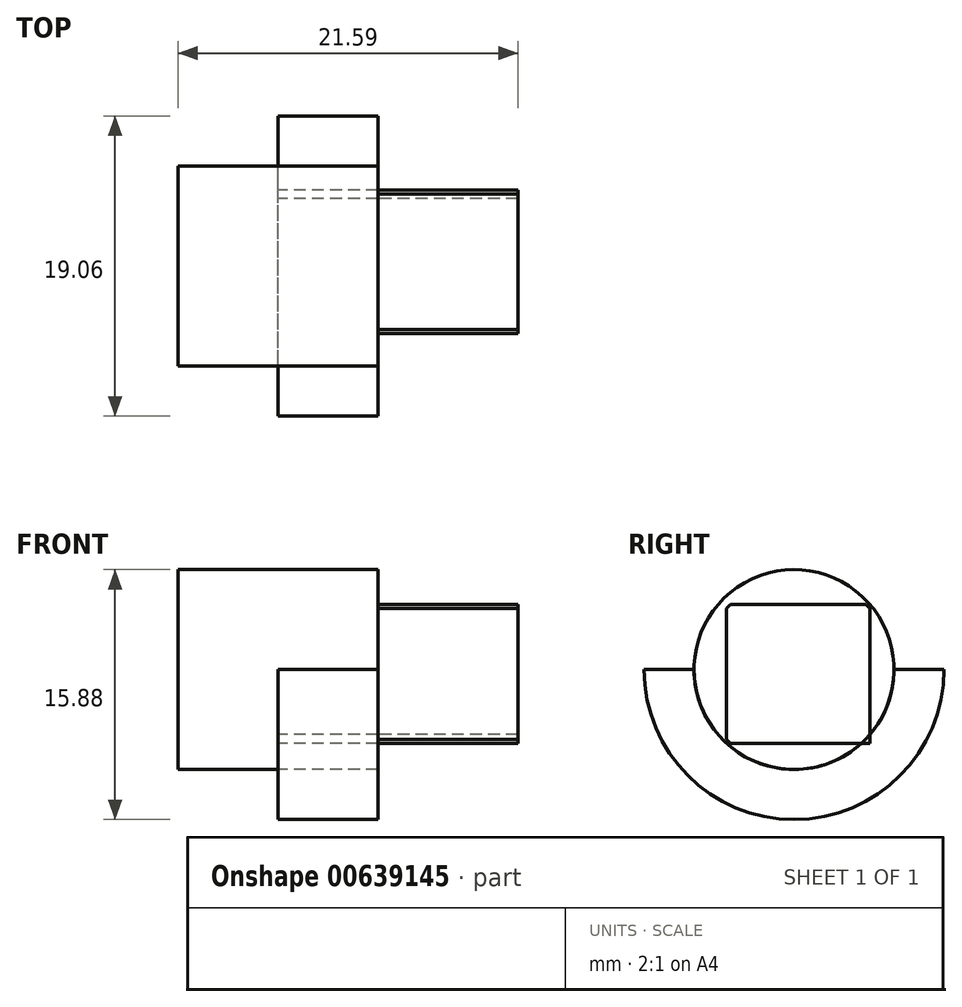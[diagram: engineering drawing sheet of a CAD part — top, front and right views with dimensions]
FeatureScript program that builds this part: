
annotation { "Feature Type Name" : "Feature", "Feature Type Description" : "" }
export const myFeature = defineFeature(function(context is Context, id is Id, definition is map)
    precondition{}
    {
        {
            var Q0;
            Q0=qCreatedBy(makeId("Right.planeOp"),FACE);
            var sketch = newSketch(context, id + "F0", { "sketchPlane" : qUnion([Q0])});
            skCircle(sketch, "E0.0", {"center": v(0, 0) * mm, "radius": 9.53 * mm});
            skLineSegment(sketch, "E1", {"start": v(0, 15.48) * mm, "end": v(0, -15.3) * mm});
            skLineSegment(sketch, "E2", {"start": v(-13.6, 0) * mm, "end": v(13.58, 0) * mm});
            skArc(sketch, "E3", {"start": v(4.83, 4.12) * mm, "mid": v(-4.4, 4.57) * mm, "end": v(-4.3, -4.68) * mm});
            skArc(sketch, "E4", {"start": v(3.74, -5.13) * mm, "mid": v(6.3, -0.75) * mm, "end": v(4.83, 4.12) * mm});
            skArc(sketch, "E5", {"start": v(-3.35, -5.4) * mm, "mid": v(0.23, -6.35) * mm, "end": v(3.74, -5.13) * mm});
            skArc(sketch, "E6", {"start": v(-4.3, -4.68) * mm, "mid": v(-3.84, -5.06) * mm, "end": v(-3.35, -5.4) * mm});
            skLineSegment(sketch, "E7.bottom", {"start": v(-4.3, -4.68) * mm, "end": v(4.83, -4.68) * mm});
            skLineSegment(sketch, "E7.top", {"start": v(-4.3, 4.12) * mm, "end": v(4.83, 4.12) * mm});
            skLineSegment(sketch, "E7.left", {"start": v(-4.3, -4.68) * mm, "end": v(-4.3, 4.12) * mm});
            skLineSegment(sketch, "E7.right", {"start": v(4.83, -4.68) * mm, "end": v(4.83, 4.12) * mm});
            skSolve(sketch);
        }
        {
            var Q0;
            Q0=makeQuery(id+"F0.imprint","IMPRINT",FACE,{"disambiguationData":[TD([[makeQuery(id+"F0.imprint","IMPRINT",EDGE,{"derivedFrom":sQuery(id+"F0.wireOp",EDGE,"618758c0-8dd7-410c-af1e-bdc083f21560")}),1.0]])]});
            var Q1;
            {var subQ0=sQuery(id+"F0.wireOp",EDGE,"E7.bottom");var subQ1=sQuery(id+"F0.wireOp",EDGE,"E1");var subQ2=makeQuery(id+"F0.imprint","INTERSECT",VERTEX,{"derivedFrom":[subQ1,subQ0]});Q1=makeQuery(id+"F0.imprint","IMPRINT",FACE,{"disambiguationData":[TD([[makeQuery(id+"F0.imprint","IMPRINT",EDGE,{"disambiguationData":[TD([[subQ2,-1.0]])],"derivedFrom":subQ1}),1.0]])]});}
            var Q2;
            {var subQ5=sQuery(id+"F0.wireOp",EDGE,"E2");var subQ6=sQuery(id+"F0.wireOp",EDGE,"E1");var subQ7=makeQuery(id+"F0.imprint","INTERSECT",VERTEX,{"derivedFrom":[subQ6,subQ5]});Q2=makeQuery(id+"F0.imprint","IMPRINT",FACE,{"disambiguationData":[TD([[makeQuery(id+"F0.imprint","IMPRINT",EDGE,{"disambiguationData":[TD([[subQ7,-1.0]])],"derivedFrom":subQ6}),1.0]])]});}
            var Q3;
            {var subQ0=sQuery(id+"F0.wireOp",EDGE,"E7.top");var subQ1=sQuery(id+"F0.wireOp",EDGE,"E1");var subQ2=makeQuery(id+"F0.imprint","INTERSECT",VERTEX,{"derivedFrom":[subQ1,subQ0]});Q3=makeQuery(id+"F0.imprint","IMPRINT",FACE,{"disambiguationData":[TD([[makeQuery(id+"F0.imprint","IMPRINT",EDGE,{"disambiguationData":[TD([[subQ2,-1.0]])],"derivedFrom":subQ1}),1.0]])]});}
            var Q4;
            {var subQ0=sQuery(id+"F0.wireOp",EDGE,"E7.top");var subQ1=sQuery(id+"F0.wireOp",EDGE,"E1");var subQ2=makeQuery(id+"F0.imprint","INTERSECT",VERTEX,{"derivedFrom":[subQ1,subQ0]});Q4=makeQuery(id+"F0.imprint","IMPRINT",FACE,{"disambiguationData":[TD([[makeQuery(id+"F0.imprint","IMPRINT",EDGE,{"disambiguationData":[TD([[subQ2,-1.0]])],"derivedFrom":subQ1}),-1.0]])]});}
            var Q5;
            {var subQ0=sQuery(id+"F0.wireOp",EDGE,"E2");var subQ1=sQuery(id+"F0.wireOp",EDGE,"E1");var subQ2=makeQuery(id+"F0.imprint","INTERSECT",VERTEX,{"derivedFrom":[subQ1,subQ0]});Q5=makeQuery(id+"F0.imprint","IMPRINT",FACE,{"disambiguationData":[TD([[makeQuery(id+"F0.imprint","IMPRINT",EDGE,{"disambiguationData":[TD([[subQ2,-1.0]])],"derivedFrom":subQ1}),-1.0]])]});}
            var Q6;
            {var subQ0=sQuery(id+"F0.wireOp",EDGE,"E3");var subQ1=sQuery(id+"F0.wireOp",EDGE,"E2");var subQ2=makeQuery(id+"F0.imprint","INTERSECT",VERTEX,{"derivedFrom":[subQ1,subQ0]});Q6=makeQuery(id+"F0.imprint","IMPRINT",FACE,{"disambiguationData":[TD([[makeQuery(id+"F0.imprint","IMPRINT",EDGE,{"disambiguationData":[TD([[subQ2,-1.0]])],"derivedFrom":subQ1}),-1.0]])]});}
            var Q7;
            {var subQ5=sQuery(id+"F0.wireOp",EDGE,"E6");Q7=makeQuery(id+"F0.imprint","IMPRINT",FACE,{"disambiguationData":[TD([[makeQuery(id+"F0.imprint","IMPRINT",EDGE,{"derivedFrom":subQ5}),1.0]])]});}
            var Q8;
            {var subQ0=sQuery(id+"F0.wireOp",EDGE,"E7.right");var subQ1=sQuery(id+"F0.wireOp",EDGE,"E2");var subQ2=makeQuery(id+"F0.imprint","INTERSECT",VERTEX,{"derivedFrom":[subQ1,subQ0]});Q8=makeQuery(id+"F0.imprint","IMPRINT",FACE,{"disambiguationData":[TD([[makeQuery(id+"F0.imprint","IMPRINT",EDGE,{"disambiguationData":[TD([[subQ2,-1.0]])],"derivedFrom":subQ1}),1.0]])]});}
            var Q9;
            {var subQ0=sQuery(id+"F0.wireOp",EDGE,"E7.right");var subQ1=sQuery(id+"F0.wireOp",EDGE,"E2");var subQ2=makeQuery(id+"F0.imprint","INTERSECT",VERTEX,{"derivedFrom":[subQ1,subQ0]});Q9=makeQuery(id+"F0.imprint","IMPRINT",FACE,{"disambiguationData":[TD([[makeQuery(id+"F0.imprint","IMPRINT",EDGE,{"disambiguationData":[TD([[subQ2,-1.0]])],"derivedFrom":subQ1}),-1.0]])]});}
            var Q10;
            {var subQ0=sQuery(id+"F0.wireOp",EDGE,"E3");var subQ1=sQuery(id+"F0.wireOp",EDGE,"E1");var subQ2=makeQuery(id+"F0.imprint","INTERSECT",VERTEX,{"derivedFrom":[subQ1,subQ0]});Q10=makeQuery(id+"F0.imprint","IMPRINT",FACE,{"disambiguationData":[TD([[makeQuery(id+"F0.imprint","IMPRINT",EDGE,{"disambiguationData":[TD([[subQ2,-1.0]])],"derivedFrom":subQ1}),1.0]])]});}
            var Q11;
            {var subQ3=sQuery(id+"F0.wireOp",EDGE,"E1");var subQ5=sQuery(id+"F0.wireOp",EDGE,"E3");var subQ6=makeQuery(id+"F0.imprint","INTERSECT",VERTEX,{"derivedFrom":[subQ3,subQ5]});Q11=makeQuery(id+"F0.imprint","IMPRINT",FACE,{"disambiguationData":[TD([[makeQuery(id+"F0.imprint","IMPRINT",EDGE,{"disambiguationData":[TD([[subQ6,-1.0]])],"derivedFrom":subQ3}),-1.0]])]});}
            extrude(context, id + "F1", {"entities" : qUnion([Q0, Q1, Q2, Q3, Q4, Q5, Q6, Q7, Q8, Q9, Q10, Q11]), "depth" : 6.35 * mm, "offsetDistance" : 25.4 * mm, "hasSecondDirection" : true, "secondDirectionOppositeDirection" : true, "secondDirectionDepth" : 6.35 * mm});
        }
        {
            var Q0;
            {var subQ0=sQuery(id+"F0.wireOp",EDGE,"E2");var subQ1=sQuery(id+"F0.wireOp",EDGE,"E0.0");var subQ2=makeQuery(id+"F0.imprint","INTERSECT",VERTEX,{"disambiguationData":[OD(0.0)],"derivedFrom":[subQ1,subQ0]});Q0=makeQuery(id+"F0.imprint","IMPRINT",FACE,{"disambiguationData":[TD([[makeQuery(id+"F0.imprint","IMPRINT",EDGE,{"disambiguationData":[TD([[subQ2,1.0]])],"derivedFrom":subQ1}),1.0]])]});}
            var Q1;
            {var subQ3=sQuery(id+"F0.wireOp",EDGE,"E1");var subQ5=sQuery(id+"F0.wireOp",EDGE,"E0.0");var subQ6=makeQuery(id+"F0.imprint","INTERSECT",VERTEX,{"disambiguationData":[OD(0.0)],"derivedFrom":[subQ5,subQ3]});Q1=makeQuery(id+"F0.imprint","IMPRINT",FACE,{"disambiguationData":[TD([[makeQuery(id+"F0.imprint","IMPRINT",EDGE,{"disambiguationData":[TD([[subQ6,1.0]])],"derivedFrom":subQ5}),1.0]])]});}
            var Q2;
            {var subQ0=sQuery(id+"F0.wireOp",EDGE,"E1");var subQ1=sQuery(id+"F0.wireOp",EDGE,"E0.0");var subQ2=makeQuery(id+"F0.imprint","INTERSECT",VERTEX,{"disambiguationData":[OD(0.0)],"derivedFrom":[subQ1,subQ0]});Q2=makeQuery(id+"F0.imprint","IMPRINT",FACE,{"disambiguationData":[TD([[makeQuery(id+"F0.imprint","IMPRINT",EDGE,{"disambiguationData":[TD([[subQ2,-1.0]])],"derivedFrom":subQ1}),1.0]])]});}
            var Q3;
            {var subQ0=sQuery(id+"F0.wireOp",EDGE,"E6");Q3=makeQuery(id+"F0.imprint","IMPRINT",FACE,{"disambiguationData":[TD([[makeQuery(id+"F0.imprint","IMPRINT",EDGE,{"derivedFrom":subQ0}),-1.0]])]});}
            extrude(context, id + "F2", {"entities" : qUnion([Q0, Q1, Q2, Q3]), "depth" : 6.35 * mm, "offsetDistance" : 25.4 * mm, "hasSecondDirection" : true, "secondDirectionOppositeDirection" : false, "secondDirectionDepth" : 0 * mm});
        }
        {
            var Q0;
            {var subQ5=sQuery(id+"F0.wireOp",EDGE,"E2");var subQ6=sQuery(id+"F0.wireOp",EDGE,"E1");var subQ7=makeQuery(id+"F0.imprint","INTERSECT",VERTEX,{"derivedFrom":[subQ6,subQ5]});Q0=makeQuery(id+"F0.imprint","IMPRINT",FACE,{"disambiguationData":[TD([[makeQuery(id+"F0.imprint","IMPRINT",EDGE,{"disambiguationData":[TD([[subQ7,-1.0]])],"derivedFrom":subQ6}),1.0]])]});}
            var Q1;
            {var subQ0=sQuery(id+"F0.wireOp",EDGE,"E7.top");var subQ1=sQuery(id+"F0.wireOp",EDGE,"E1");var subQ2=makeQuery(id+"F0.imprint","INTERSECT",VERTEX,{"derivedFrom":[subQ1,subQ0]});Q1=makeQuery(id+"F0.imprint","IMPRINT",FACE,{"disambiguationData":[TD([[makeQuery(id+"F0.imprint","IMPRINT",EDGE,{"disambiguationData":[TD([[subQ2,-1.0]])],"derivedFrom":subQ1}),1.0]])]});}
            var Q2;
            {var subQ0=sQuery(id+"F0.wireOp",EDGE,"E7.top");var subQ1=sQuery(id+"F0.wireOp",EDGE,"E1");var subQ2=makeQuery(id+"F0.imprint","INTERSECT",VERTEX,{"derivedFrom":[subQ1,subQ0]});Q2=makeQuery(id+"F0.imprint","IMPRINT",FACE,{"disambiguationData":[TD([[makeQuery(id+"F0.imprint","IMPRINT",EDGE,{"disambiguationData":[TD([[subQ2,-1.0]])],"derivedFrom":subQ1}),-1.0]])]});}
            var Q3;
            {var subQ0=sQuery(id+"F0.wireOp",EDGE,"E2");var subQ1=sQuery(id+"F0.wireOp",EDGE,"E1");var subQ2=makeQuery(id+"F0.imprint","INTERSECT",VERTEX,{"derivedFrom":[subQ1,subQ0]});Q3=makeQuery(id+"F0.imprint","IMPRINT",FACE,{"disambiguationData":[TD([[makeQuery(id+"F0.imprint","IMPRINT",EDGE,{"disambiguationData":[TD([[subQ2,-1.0]])],"derivedFrom":subQ1}),-1.0]])]});}
            extrude(context, id + "F3", {"entities" : qUnion([Q0, Q1, Q2, Q3]), "depth" : 15.24 * mm, "offsetDistance" : 25.4 * mm, "hasSecondDirection" : true, "secondDirectionOppositeDirection" : false, "secondDirectionDepth" : 6.35 * mm});
        }
        {
            var Q0;
            Q0=makeQuery(id+"F3.opExtrude","SWEPT_EDGE",EDGE,{"disambiguationData":[OSD([sQuery(id+"F0.wireOp",EDGE,"E7.top"),sQuery(id+"F0.wireOp",EDGE,"E7.left")])]});
            var Q1;
            Q1=makeQuery(id+"F3.opExtrude","SWEPT_EDGE",EDGE,{"disambiguationData":[OSD([sQuery(id+"F0.wireOp",EDGE,"E3"),sQuery(id+"F0.wireOp",EDGE,"E6"),sQuery(id+"F0.wireOp",EDGE,"E7.bottom"),sQuery(id+"F0.wireOp",EDGE,"E7.left")])]});
            var Q2;
            Q2=makeQuery(id+"F3.opExtrude","SWEPT_EDGE",EDGE,{"disambiguationData":[OSD([sQuery(id+"F0.wireOp",EDGE,"E3"),sQuery(id+"F0.wireOp",EDGE,"E4"),sQuery(id+"F0.wireOp",EDGE,"E7.top"),sQuery(id+"F0.wireOp",EDGE,"E7.right")])]});
            chamfer(context, id + "F4", {"entities" : qUnion([Q0, Q1, Q2]), "width" : 0.25 * mm, "tangentPropagation" : true});
        }
    });
